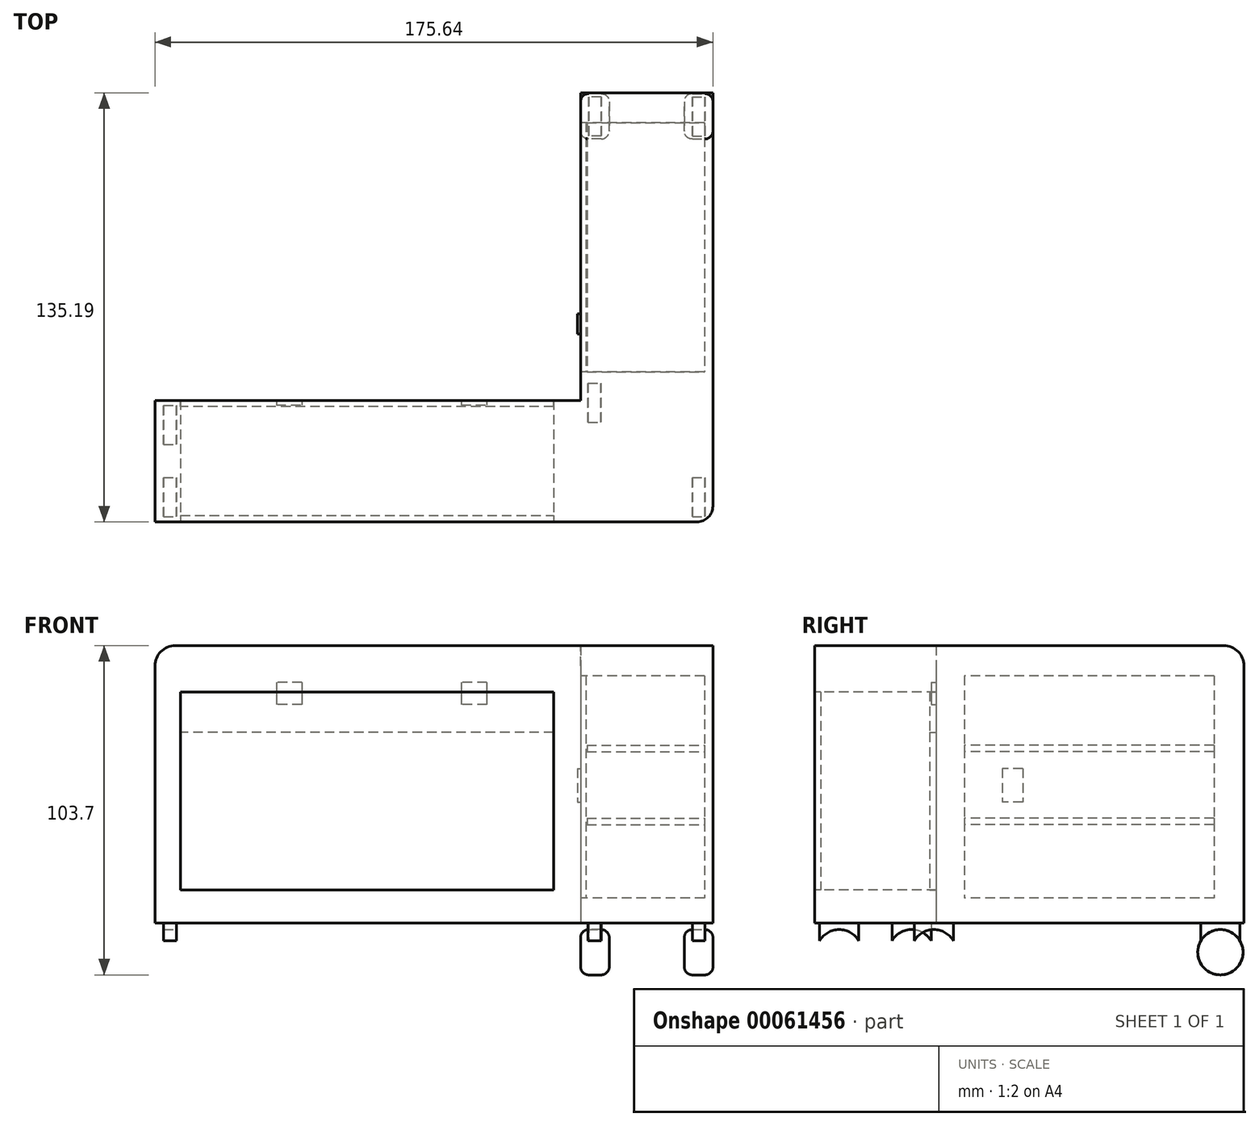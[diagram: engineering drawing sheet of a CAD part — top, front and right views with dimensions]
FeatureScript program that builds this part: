
annotation { "Feature Type Name" : "Feature", "Feature Type Description" : "" }
export const myFeature = defineFeature(function(context is Context, id is Id, definition is map)
    precondition{}
    {
        {
            var Q0;
            Q0=qCreatedBy(makeId("Front.planeOp"),FACE);
            var sketch = newSketch(context, id + "F0", { "sketchPlane" : qUnion([Q0])});
            skLineSegment(sketch, "E0.rect.bottom", {"start": v(-60.65, 49.22) * mm, "end": v(67, 49.22) * mm});
            skLineSegment(sketch, "E0.rect.left", {"start": v(-67, 42.87) * mm, "end": v(-67, -38.15) * mm});
            skLineSegment(sketch, "E0.rect.right", {"start": v(67, 49.22) * mm, "end": v(67, -38.15) * mm});
            skPoint(sketch, "E0.rect.middle", {"position": v(0, 0) * mm});
            skPoint(sketch, "E1.visualSharp", {"position": v(-67, 49.22) * mm});
            skArc(sketch, "E1.filletArc", {"start": v(-60.65, 49.22) * mm, "mid": v(-65.14, 47.36) * mm, "end": v(-67, 42.87) * mm});
            skLineSegment(sketch, "E2", {"start": v(-67, -38.15) * mm, "end": v(67, -38.15) * mm});
            skPoint(sketch, "E0.rect.top.start.orphan", {"position": v(-67, -49.22) * mm});
            skPoint(sketch, "E3.orphan", {"position": v(67, -49.22) * mm});
            skSolve(sketch);
        }
        {
            var Q0;
            Q0=makeQuery(id+"F0.imprint","IMPRINT",FACE,{"disambiguationData":[TD([[makeQuery(id+"F0.imprint","IMPRINT",EDGE,{"derivedFrom":sQuery(id+"F0.wireOp",EDGE,"E0.rect.bottom")}),-1.0]])]});
            extrude(context, id + "F1", {"entities" : qUnion([Q0]), "depth" : 38.28 * mm});
        }
        {
            var Q0;
            Q0=makeQuery(id+"F1.opExtrude","CAP_FACE",FACE,{"disambiguationData":[OSD([sQuery(id+"F0.wireOp",EDGE,"E0.rect.bottom"),sQuery(id+"F0.wireOp",EDGE,"E0.rect.left"),sQuery(id+"F0.wireOp",EDGE,"E0.rect.right"),sQuery(id+"F0.wireOp",EDGE,"E1.filletArc"),sQuery(id+"F0.wireOp",EDGE,"E2")])],"isStart":false});
            var sketch = newSketch(context, id + "F2", { "sketchPlane" : qUnion([Q0])});
            skLineSegment(sketch, "E4.bottom", {"start": v(-58.97, 34.69) * mm, "end": v(58.47, 34.69) * mm});
            skLineSegment(sketch, "E4.top", {"start": v(-58.97, -27.7) * mm, "end": v(58.47, -27.7) * mm});
            skLineSegment(sketch, "E4.left", {"start": v(-58.97, 34.69) * mm, "end": v(-58.97, -27.7) * mm});
            skLineSegment(sketch, "E4.right", {"start": v(58.47, 34.69) * mm, "end": v(58.47, -27.7) * mm});
            skSolve(sketch);
        }
        {
            var Q0;
            Q0 = qSketchRegion(id + "F2", true);
            extrude(context, id + "F3", {"entities" : qUnion([Q0]), "operationType" : NewBodyOperationType.REMOVE, "endBound" : BoundingType.THROUGH_ALL, "oppositeDirection" : true, "depth" : 25 * mm});
        }
        {
            var Q0;
            Q0=makeQuery(id+"F1.opExtrude","CAP_FACE",FACE,{"disambiguationData":[OSD([sQuery(id+"F0.wireOp",EDGE,"E0.rect.bottom"),sQuery(id+"F0.wireOp",EDGE,"E0.rect.left"),sQuery(id+"F0.wireOp",EDGE,"E0.rect.right"),sQuery(id+"F0.wireOp",EDGE,"E1.filletArc"),sQuery(id+"F0.wireOp",EDGE,"E2")])],"isStart":false});
            var sketch = newSketch(context, id + "F4", { "sketchPlane" : qUnion([Q0])});
            skLineSegment(sketch, "E5.0", {"start": v(-58.97, 34.69) * mm, "end": v(58.47, 34.69) * mm});
            skLineSegment(sketch, "E6.0", {"start": v(-58.97, 34.69) * mm, "end": v(-58.97, -27.7) * mm});
            skLineSegment(sketch, "E7.0", {"start": v(-58.97, -27.7) * mm, "end": v(58.47, -27.7) * mm});
            skLineSegment(sketch, "E8.0", {"start": v(58.47, 34.69) * mm, "end": v(58.47, -27.7) * mm});
            skSolve(sketch);
        }
        {
            var Q0;
            Q0=makeQuery(id+"F4.imprint","IMPRINT",FACE,{"disambiguationData":[TD([[makeQuery(id+"F4.imprint","IMPRINT",EDGE,{"derivedFrom":sQuery(id+"F4.wireOp",EDGE,"E5.0")}),-1.0]])]});
            extrude(context, id + "F5", {"entities" : qUnion([Q0]), "oppositeDirection" : true, "depth" : 2 * mm});
        }
        {
            var Q0;
            Q0=makeQuery(id+"F1.opExtrude","CAP_FACE",FACE,{"disambiguationData":[OSD([sQuery(id+"F0.wireOp",EDGE,"E0.rect.bottom"),sQuery(id+"F0.wireOp",EDGE,"E0.rect.left"),sQuery(id+"F0.wireOp",EDGE,"E0.rect.right"),sQuery(id+"F0.wireOp",EDGE,"E1.filletArc"),sQuery(id+"F0.wireOp",EDGE,"E2")])],"isStart":true});
            var sketch = newSketch(context, id + "F6", { "sketchPlane" : qUnion([Q0])});
            skLineSegment(sketch, "E9.0", {"start": v(-58.47, 21.87) * mm, "end": v(-58.47, -27.7) * mm});
            skLineSegment(sketch, "E10.0", {"start": v(58.97, -27.7) * mm, "end": v(-58.47, -27.7) * mm});
            skLineSegment(sketch, "E11.0", {"start": v(58.97, 21.87) * mm, "end": v(58.97, -27.7) * mm});
            skLineSegment(sketch, "E12", {"start": v(-58.47, 21.87) * mm, "end": v(58.97, 21.87) * mm});
            skPoint(sketch, "E13.0.end.orphan", {"position": v(-58.47, 34.69) * mm});
            skPoint(sketch, "E14.orphan", {"position": v(58.97, 34.69) * mm});
            skSolve(sketch);
        }
        {
            var Q0;
            Q0=makeQuery(id+"F6.imprint","IMPRINT",FACE,{"disambiguationData":[TD([[makeQuery(id+"F6.imprint","IMPRINT",EDGE,{"derivedFrom":sQuery(id+"F6.wireOp",EDGE,"E9.0")}),1.0]])]});
            extrude(context, id + "F7", {"entities" : qUnion([Q0]), "oppositeDirection" : true, "depth" : 2 * mm});
        }
        {
            var Q0;
            Q0=makeQuery(id+"F1.opExtrude","CAP_FACE",FACE,{"disambiguationData":[OSD([sQuery(id+"F0.wireOp",EDGE,"E0.rect.bottom"),sQuery(id+"F0.wireOp",EDGE,"E0.rect.left"),sQuery(id+"F0.wireOp",EDGE,"E0.rect.right"),sQuery(id+"F0.wireOp",EDGE,"E1.filletArc"),sQuery(id+"F0.wireOp",EDGE,"E2")])],"isStart":true});
            var sketch = newSketch(context, id + "F8", { "sketchPlane" : qUnion([Q0])});
            skLineSegment(sketch, "E15.0", {"start": v(58.97, 34.69) * mm, "end": v(-58.47, 34.69) * mm});
            skLineSegment(sketch, "E16.0", {"start": v(-58.47, 34.69) * mm, "end": v(-58.47, 21.87) * mm});
            skLineSegment(sketch, "E17.0", {"start": v(-58.47, 21.87) * mm, "end": v(58.97, 21.87) * mm});
            skLineSegment(sketch, "E18.0", {"start": v(58.97, 34.69) * mm, "end": v(58.97, 21.87) * mm});
            skPoint(sketch, "E19.orphan", {"position": v(-58.47, -27.7) * mm});
            skPoint(sketch, "E20.orphan", {"position": v(58.97, -27.7) * mm});
            skSolve(sketch);
        }
        {
            var Q0;
            Q0=makeQuery(id+"F8.imprint","IMPRINT",FACE,{"disambiguationData":[TD([[makeQuery(id+"F8.imprint","IMPRINT",EDGE,{"derivedFrom":sQuery(id+"F8.wireOp",EDGE,"E15.0")}),1.0]])]});
            extrude(context, id + "F9", {"entities" : qUnion([Q0]), "oppositeDirection" : true, "depth" : 2 * mm});
        }
        {
            var Q0;
            Q0=makeQuery(id+"F1.opExtrude","CAP_FACE",FACE,{"disambiguationData":[OSD([sQuery(id+"F0.wireOp",EDGE,"E0.rect.bottom"),sQuery(id+"F0.wireOp",EDGE,"E0.rect.left"),sQuery(id+"F0.wireOp",EDGE,"E0.rect.right"),sQuery(id+"F0.wireOp",EDGE,"E1.filletArc"),sQuery(id+"F0.wireOp",EDGE,"E2")])],"isStart":true});
            cPlane(context, id + "F10", {"entities" : qUnion([Q0]), "cplaneType" : CPlaneType.OFFSET, "offset" : 0 * mm, "width" : 150 * mm, "height" : 150 * mm});
        }
        {
            var Q0;
            Q0=qCreatedBy(id+"F10.planeOp",FACE);
            var sketch = newSketch(context, id + "F11", { "sketchPlane" : qUnion([Q0])});
            skLineSegment(sketch, "E21.bottom", {"start": v(-37.46, 37.7) * mm, "end": v(-29.46, 37.7) * mm});
            skLineSegment(sketch, "E21.top", {"start": v(-37.46, 30.7) * mm, "end": v(-29.46, 30.7) * mm});
            skLineSegment(sketch, "E21.left", {"start": v(-37.46, 37.7) * mm, "end": v(-37.46, 30.7) * mm});
            skLineSegment(sketch, "E21.right", {"start": v(-29.46, 37.7) * mm, "end": v(-29.46, 30.7) * mm});
            skPoint(sketch, "E22.firstSnap0", {"position": v(-33.46, 37.7) * mm});
            skLineSegment(sketch, "E22.bottom", {"start": v(20.75, 37.7) * mm, "end": v(28.75, 37.7) * mm});
            skLineSegment(sketch, "E22.top", {"start": v(20.75, 30.7) * mm, "end": v(28.75, 30.7) * mm});
            skLineSegment(sketch, "E22.left", {"start": v(20.75, 37.7) * mm, "end": v(20.75, 30.7) * mm});
            skLineSegment(sketch, "E22.right", {"start": v(28.75, 37.7) * mm, "end": v(28.75, 30.7) * mm});
            skSolve(sketch);
        }
        {
            var Q0;
            Q0=makeQuery(id+"F11.imprint","IMPRINT",FACE,{"disambiguationData":[TD([[makeQuery(id+"F11.imprint","IMPRINT",EDGE,{"derivedFrom":sQuery(id+"F11.wireOp",EDGE,"E21.bottom")}),-1.0]])]});
            var Q1;
            Q1=makeQuery(id+"F11.imprint","IMPRINT",FACE,{"disambiguationData":[TD([[makeQuery(id+"F11.imprint","IMPRINT",EDGE,{"derivedFrom":sQuery(id+"F11.wireOp",EDGE,"E22.bottom")}),-1.0]])]});
            extrude(context, id + "F12", {"entities" : qUnion([Q0, Q1]), "operationType" : NewBodyOperationType.REMOVE, "oppositeDirection" : true, "depth" : 1.5 * mm});
        }
        {
            var Q0;
            Q0=qCreatedBy(id+"F10.planeOp",FACE);
            var sketch = newSketch(context, id + "F13", { "sketchPlane" : qUnion([Q0])});
            skLineSegment(sketch, "E23.0", {"start": v(-37.46, 37.7) * mm, "end": v(-29.46, 37.7) * mm});
            skLineSegment(sketch, "E24.0", {"start": v(-37.46, 37.7) * mm, "end": v(-37.46, 34.69) * mm});
            skLineSegment(sketch, "E25.0", {"start": v(-37.46, 34.69) * mm, "end": v(-37.46, 30.7) * mm});
            skLineSegment(sketch, "E26.0", {"start": v(-37.46, 30.7) * mm, "end": v(-29.46, 30.7) * mm});
            skLineSegment(sketch, "E27.0", {"start": v(-29.46, 34.69) * mm, "end": v(-29.46, 30.7) * mm});
            skLineSegment(sketch, "E28.0", {"start": v(-29.46, 37.7) * mm, "end": v(-29.46, 34.69) * mm});
            skLineSegment(sketch, "E29.0", {"start": v(20.75, 37.7) * mm, "end": v(20.75, 34.69) * mm});
            skLineSegment(sketch, "E30.0", {"start": v(20.75, 37.7) * mm, "end": v(28.75, 37.7) * mm});
            skLineSegment(sketch, "E31.0", {"start": v(28.75, 37.7) * mm, "end": v(28.75, 34.69) * mm});
            skLineSegment(sketch, "E32.0", {"start": v(28.75, 34.69) * mm, "end": v(28.75, 30.7) * mm});
            skLineSegment(sketch, "E33.0", {"start": v(20.75, 30.7) * mm, "end": v(28.75, 30.7) * mm});
            skLineSegment(sketch, "E34.0.0", {"start": v(20.75, 34.69) * mm, "end": v(20.75, 30.7) * mm});
            skLineSegment(sketch, "E34.0.2", {"start": v(28.75, 30.7) * mm, "end": v(28.75, 34.69) * mm});
            skSolve(sketch);
        }
        {
            var Q0;
            Q0=makeQuery(id+"F13.imprint","IMPRINT",FACE,{"disambiguationData":[TD([[makeQuery(id+"F13.imprint","IMPRINT",EDGE,{"derivedFrom":sQuery(id+"F13.wireOp",EDGE,"E23.0")}),-1.0]])]});
            var Q1;
            Q1=makeQuery(id+"F13.imprint","IMPRINT",FACE,{"disambiguationData":[TD([[makeQuery(id+"F13.imprint","IMPRINT",EDGE,{"derivedFrom":sQuery(id+"F13.wireOp",EDGE,"E29.0")}),1.0]])]});
            extrude(context, id + "F14", {"entities" : qUnion([Q0, Q1]), "oppositeDirection" : true, "depth" : 1.5 * mm});
        }
        {
            var Q0;
            Q0=makeQuery(id+"F1.opExtrude","SWEPT_FACE",FACE,{"disambiguationData":[OSD([sQuery(id+"F0.wireOp",EDGE,"E0.rect.right")])]});
            cPlane(context, id + "F15", {"entities" : qUnion([Q0]), "cplaneType" : CPlaneType.OFFSET, "offset" : 0 * mm, "width" : 150 * mm, "height" : 150 * mm});
        }
        {
            var Q0;
            Q0=qCreatedBy(id+"F15.planeOp",FACE);
            var sketch = newSketch(context, id + "F16", { "sketchPlane" : qUnion([Q0])});
            skLineSegment(sketch, "E35.0", {"start": v(-38.28, 49.22) * mm, "end": v(0, 49.22) * mm});
            skLineSegment(sketch, "E36.0", {"start": v(-38.28, 49.22) * mm, "end": v(-38.28, -38.15) * mm});
            skLineSegment(sketch, "E37.0", {"start": v(-38.28, -38.15) * mm, "end": v(0, -38.15) * mm});
            skLineSegment(sketch, "E38", {"start": v(0, 49.22) * mm, "end": v(90.56, 49.22) * mm});
            skLineSegment(sketch, "E39", {"start": v(96.9, -38.15) * mm, "end": v(0, -38.15) * mm});
            skLineSegment(sketch, "E40", {"start": v(96.9, 42.87) * mm, "end": v(96.9, -38.15) * mm});
            skPoint(sketch, "E41.visualSharp", {"position": v(96.9, 49.22) * mm});
            skArc(sketch, "E41.filletArc", {"start": v(96.9, 42.87) * mm, "mid": v(95.05, 47.36) * mm, "end": v(90.56, 49.22) * mm});
            skSolve(sketch);
        }
        {
            var Q0;
            Q0=makeQuery(id+"F16.imprint","IMPRINT",FACE,{"disambiguationData":[TD([[makeQuery(id+"F16.imprint","IMPRINT",EDGE,{"derivedFrom":sQuery(id+"F16.wireOp",EDGE,"E35.0")}),-1.0]])]});
            extrude(context, id + "F17", {"entities" : qUnion([Q0]), "operationType" : NewBodyOperationType.ADD, "depth" : 41.64 * mm});
        }
        {
            var Q0;
            Q0=makeQuery(id+"F17.opExtrude","CAP_EDGE",EDGE,{"disambiguationData":[OSD([sQuery(id+"F16.wireOp",EDGE,"E36.0")])],"isStart":false});
            fillet(context, id + "F18", {"entities" : qUnion([Q0]), "radius" : 5 * mm, "tangentPropagation" : true, "allowEdgeOverflow" : false});
        }
        {
            var Q0;
            Q0=makeQuery(id+"F17.opExtrude","CAP_FACE",FACE,{"disambiguationData":[OSD([sQuery(id+"F16.wireOp",EDGE,"E35.0"),sQuery(id+"F16.wireOp",EDGE,"E36.0"),sQuery(id+"F16.wireOp",EDGE,"E37.0"),sQuery(id+"F16.wireOp",EDGE,"E38"),sQuery(id+"F16.wireOp",EDGE,"E39"),sQuery(id+"F16.wireOp",EDGE,"E40"),sQuery(id+"F16.wireOp",EDGE,"E41.filletArc")])],"isStart":true});
            var sketch = newSketch(context, id + "F19", { "sketchPlane" : qUnion([Q0])});
            skLineSegment(sketch, "E42.bottom", {"start": v(-87.48, 39.73) * mm, "end": v(-8.92, 39.73) * mm});
            skLineSegment(sketch, "E42.top", {"start": v(-87.48, -30.33) * mm, "end": v(-8.92, -30.33) * mm});
            skLineSegment(sketch, "E42.left", {"start": v(-87.48, 39.73) * mm, "end": v(-87.48, -30.33) * mm});
            skLineSegment(sketch, "E42.right", {"start": v(-8.92, 39.73) * mm, "end": v(-8.92, -30.33) * mm});
            skSolve(sketch);
        }
        {
            var Q0;
            Q0 = qSketchRegion(id + "F19", true);
            extrude(context, id + "F20", {"entities" : qUnion([Q0]), "operationType" : NewBodyOperationType.REMOVE, "oppositeDirection" : true, "depth" : 39 * mm});
        }
        {
            var Q0;
            Q0=makeQuery(id+"F20.boolean.opBoolean","COPY",FACE,{"derivedFrom":makeQuery(id+"F20.opExtrude","CAP_FACE",FACE,{"disambiguationData":[OSD([sQuery(id+"F19.wireOp",EDGE,"E42.bottom"),sQuery(id+"F19.wireOp",EDGE,"E42.top"),sQuery(id+"F19.wireOp",EDGE,"E42.left"),sQuery(id+"F19.wireOp",EDGE,"E42.right")])],"isStart":false})});
            var sketch = newSketch(context, id + "F21", { "sketchPlane" : qUnion([Q0])});
            skLineSegment(sketch, "E43.rect.left", {"start": v(-87.48, 15.81) * mm, "end": v(-87.48, 17.81) * mm});
            skLineSegment(sketch, "E43.rect.right", {"start": v(-8.92, 15.81) * mm, "end": v(-8.92, 17.81) * mm});
            skPoint(sketch, "E43.rect.middle", {"position": v(-48.2, 16.81) * mm});
            skLineSegment(sketch, "E44.rect.left", {"start": v(-87.48, -5.19) * mm, "end": v(-87.48, -7.19) * mm});
            skLineSegment(sketch, "E44.rect.right", {"start": v(-8.92, -5.19) * mm, "end": v(-8.92, -7.19) * mm});
            skPoint(sketch, "E44.rect.middle", {"position": v(-48.2, -6.19) * mm});
            skPoint(sketch, "E45.orphan", {"position": v(-87.48, -6.19) * mm});
            skPoint(sketch, "E46.end.orphan", {"position": v(-8.92, -6.19) * mm});
            skPoint(sketch, "E47.orphan", {"position": v(-87.48, 16.81) * mm});
            skPoint(sketch, "E48.end.orphan", {"position": v(-8.92, 16.81) * mm});
            skLineSegment(sketch, "E49", {"start": v(-8.92, 17.81) * mm, "end": v(-8.92, 15.81) * mm});
            skLineSegment(sketch, "E50", {"start": v(-87.48, 17.81) * mm, "end": v(-87.48, 15.81) * mm});
            skLineSegment(sketch, "E51.bottom", {"start": v(-87.48, 17.81) * mm, "end": v(-8.92, 17.81) * mm});
            skLineSegment(sketch, "E51.top", {"start": v(-87.48, 15.81) * mm, "end": v(-8.92, 15.81) * mm});
            skLineSegment(sketch, "E51.left", {"start": v(-87.48, 17.81) * mm, "end": v(-87.48, 16.81) * mm});
            skLineSegment(sketch, "E52.bottom", {"start": v(-87.48, -5.19) * mm, "end": v(-8.92, -5.19) * mm});
            skLineSegment(sketch, "E52.top", {"start": v(-87.48, -7.19) * mm, "end": v(-8.92, -7.19) * mm});
            skSolve(sketch);
        }
        {
            var Q0;
            {var subQ0=sQuery(id+"F21.wireOp",EDGE,"E51.bottom");Q0=makeQuery(id+"F21.imprint","IMPRINT",FACE,{"disambiguationData":[TD([[makeQuery(id+"F21.imprint","IMPRINT",EDGE,{"derivedFrom":subQ0}),-1.0]])]});}
            var Q1;
            Q1=makeQuery(id+"F21.imprint","IMPRINT",FACE,{"disambiguationData":[TD([[makeQuery(id+"F21.imprint","IMPRINT",EDGE,{"derivedFrom":sQuery(id+"F21.wireOp",EDGE,"E52.bottom")}),-1.0]])]});
            extrude(context, id + "F22", {"entities" : qUnion([Q0, Q1]), "depth" : 37 * mm});
        }
        {
            var Q0;
            Q0=makeQuery(id+"F17.opExtrude","CAP_FACE",FACE,{"disambiguationData":[OSD([sQuery(id+"F16.wireOp",EDGE,"E35.0"),sQuery(id+"F16.wireOp",EDGE,"E36.0"),sQuery(id+"F16.wireOp",EDGE,"E37.0"),sQuery(id+"F16.wireOp",EDGE,"E38"),sQuery(id+"F16.wireOp",EDGE,"E39"),sQuery(id+"F16.wireOp",EDGE,"E40"),sQuery(id+"F16.wireOp",EDGE,"E41.filletArc")])],"isStart":true});
            var sketch = newSketch(context, id + "F23", { "sketchPlane" : qUnion([Q0])});
            skLineSegment(sketch, "E53.0", {"start": v(-87.48, 39.73) * mm, "end": v(-8.92, 39.73) * mm});
            skLineSegment(sketch, "E54.0", {"start": v(-87.48, 39.73) * mm, "end": v(-87.48, -30.33) * mm});
            skLineSegment(sketch, "E55.0", {"start": v(-87.48, -30.33) * mm, "end": v(-8.92, -30.33) * mm});
            skLineSegment(sketch, "E56.0", {"start": v(-8.92, 39.73) * mm, "end": v(-8.92, -30.33) * mm});
            skSolve(sketch);
        }
        {
            var Q0;
            Q0 = qSketchRegion(id + "F23", true);
            extrude(context, id + "F24", {"entities" : qUnion([Q0]), "oppositeDirection" : true, "depth" : 1.72 * mm});
        }
        {
            var Q0;
            Q0=makeQuery(id+"F24.opExtrude","CAP_FACE",FACE,{"disambiguationData":[OSD([sQuery(id+"F23.wireOp",EDGE,"E53.0"),sQuery(id+"F23.wireOp",EDGE,"E54.0"),sQuery(id+"F23.wireOp",EDGE,"E55.0"),sQuery(id+"F23.wireOp",EDGE,"E56.0")])],"isStart":true});
            var sketch = newSketch(context, id + "F25", { "sketchPlane" : qUnion([Q0])});
            skLineSegment(sketch, "E57.bottom", {"start": v(-27.26, 10.52) * mm, "end": v(-20.85, 10.52) * mm});
            skLineSegment(sketch, "E57.top", {"start": v(-27.26, 0) * mm, "end": v(-20.85, 0) * mm});
            skLineSegment(sketch, "E57.left", {"start": v(-27.26, 10.52) * mm, "end": v(-27.26, 0) * mm});
            skLineSegment(sketch, "E57.right", {"start": v(-20.85, 10.52) * mm, "end": v(-20.85, 0) * mm});
            skSolve(sketch);
        }
        {
            var Q0;
            Q0 = qSketchRegion(id + "F25", true);
            extrude(context, id + "F26", {"entities" : qUnion([Q0]), "operationType" : NewBodyOperationType.ADD, "depth" : 1 * mm});
        }
        {
            var Q0;
            Q0=makeQuery(id+"F17.opExtrude","CAP_FACE",FACE,{"disambiguationData":[OSD([sQuery(id+"F16.wireOp",EDGE,"E35.0"),sQuery(id+"F16.wireOp",EDGE,"E36.0"),sQuery(id+"F16.wireOp",EDGE,"E37.0"),sQuery(id+"F16.wireOp",EDGE,"E38"),sQuery(id+"F16.wireOp",EDGE,"E39"),sQuery(id+"F16.wireOp",EDGE,"E40"),sQuery(id+"F16.wireOp",EDGE,"E41.filletArc")])],"isStart":false});
            var sketch = newSketch(context, id + "F27", { "sketchPlane" : qUnion([Q0])});
            skCircle(sketch, "E58", {"center": v(89.48, -47.35) * mm, "radius": 7.14 * mm});
            skSolve(sketch);
        }
        {
            var Q0;
            Q0=makeQuery(id+"F27.imprint","IMPRINT",FACE,{"disambiguationData":[TD([[makeQuery(id+"F27.imprint","IMPRINT",EDGE,{"derivedFrom":sQuery(id+"F27.wireOp",EDGE,"E58")}),1.0]])]});
            extrude(context, id + "F28", {"entities" : qUnion([Q0]), "oppositeDirection" : true, "depth" : 9 * mm});
        }
        {
            var Q0;
            Q0=makeQuery(id+"F28.opExtrude","CAP_EDGE",EDGE,{"disambiguationData":[OSD([sQuery(id+"F27.wireOp",EDGE,"E58")])],"isStart":true});
            var Q1;
            Q1=makeQuery(id+"F28.opExtrude","CAP_EDGE",EDGE,{"disambiguationData":[OSD([sQuery(id+"F27.wireOp",EDGE,"E58")])],"isStart":false});
            fillet(context, id + "F29", {"entities" : qUnion([Q0, Q1]), "radius" : 2.5 * mm, "tangentPropagation" : true, "allowEdgeOverflow" : false});
        }
        {
            var Q0;
            Q0=makeQuery(id+"F28.opExtrude","CAP_FACE",FACE,{"disambiguationData":[OSD([sQuery(id+"F27.wireOp",EDGE,"E58")])],"isStart":true});
            cPlane(context, id + "F30", {"entities" : qUnion([Q0]), "cplaneType" : CPlaneType.OFFSET, "offset" : 2.5 * mm, "oppositeDirection" : true, "width" : 150 * mm, "height" : 150 * mm});
        }
        {
            var Q0;
            Q0=qCreatedBy(id+"F30.planeOp",FACE);
            var sketch = newSketch(context, id + "F31", { "sketchPlane" : qUnion([Q0])});
            skArc(sketch, "E59.0", {"start": v(95.63, -43.73) * mm, "mid": v(89.48, -40.2) * mm, "end": v(83.32, -43.73) * mm});
            skLineSegment(sketch, "E60.0", {"start": v(83.32, -38.15) * mm, "end": v(95.63, -38.15) * mm});
            skLineSegment(sketch, "E61", {"start": v(83.32, -38.15) * mm, "end": v(83.32, -43.73) * mm});
            skLineSegment(sketch, "E62", {"start": v(95.63, -43.73) * mm, "end": v(95.63, -38.15) * mm});
            skPoint(sketch, "E63.orphan", {"position": v(-33.28, -38.15) * mm});
            skPoint(sketch, "E64.orphan", {"position": v(96.9, -38.15) * mm});
            skSolve(sketch);
        }
        {
            var Q0;
            Q0=makeQuery(id+"F31.imprint","IMPRINT",FACE,{"disambiguationData":[TD([[makeQuery(id+"F31.imprint","IMPRINT",EDGE,{"derivedFrom":sQuery(id+"F31.wireOp",EDGE,"E59.0")}),-1.0]])]});
            extrude(context, id + "F32", {"entities" : qUnion([Q0]), "oppositeDirection" : true, "depth" : 4 * mm});
        }
        {
            var Q0;
            Q0=makeQuery(id+"F17.opExtrude","SWEPT_FACE",FACE,{"disambiguationData":[OSD([sQuery(id+"F16.wireOp",EDGE,"E40")])]});
            var sketch = newSketch(context, id + "F33", { "sketchPlane" : qUnion([Q0])});
            skLineSegment(sketch, "E65.0", {"start": v(-108.64, -38.15) * mm, "end": v(-67, -38.15) * mm, "construction": true});
            skLineSegment(sketch, "E66", {"start": v(-87.82, -38.15) * mm, "end": v(-87.82, 27.49) * mm, "construction": true});
            skSolve(sketch);
        }
        {
            var Q0;
            Q0=sQuery(id+"F33.wireOp",EDGE,"E66");
            cPlane(context, id + "F34", {"entities" : qUnion([Q0]), "cplaneType" : CPlaneType.LINE_ANGLE, "offset" : 150 * mm, "angle" : 0 * degree, "width" : 150 * mm, "height" : 150 * mm});
        }
        {
            var Q0;
            Q0=makeQuery(id+"F28.opExtrude","SWEPT_BODY",BODY,{"disambiguationData":[OSD([sQuery(id+"F27.wireOp",EDGE,"E58")])]});
            var Q1;
            Q1=makeQuery(id+"F32.opExtrude","SWEPT_BODY",BODY,{"disambiguationData":[OSD([sQuery(id+"F31.wireOp",EDGE,"E59.0"),sQuery(id+"F31.wireOp",EDGE,"E60.0"),sQuery(id+"F31.wireOp",EDGE,"E61"),sQuery(id+"F31.wireOp",EDGE,"E62")])]});
            var Q2;
            Q2=qCreatedBy(id+"F34.planeOp",FACE);
            mirror(context, id + "F35", {"entities" : qUnion([Q0, Q1]), "mirrorPlane" : qUnion([Q2])});
        }
        {
            var Q0;
            Q0=makeQuery(id+"F32.opExtrude","SWEPT_BODY",BODY,{"disambiguationData":[OSD([sQuery(id+"F31.wireOp",EDGE,"E59.0"),sQuery(id+"F31.wireOp",EDGE,"E60.0"),sQuery(id+"F31.wireOp",EDGE,"E61"),sQuery(id+"F31.wireOp",EDGE,"E62")])]});
            transform(context, id + "F36", {"entities" : qUnion([Q0]), "transformType" : TransformType.TRANSLATION_3D, "dx" : 0 * mm, "dy" : -120 * mm, "dz" : 0 * mm, "makeCopy" : true});
        }
        {
            var Q0;
            Q0=makeQuery(id+"F36.opPattern","COPY",BODY,{"derivedFrom":makeQuery(id+"F32.opExtrude","SWEPT_BODY",BODY,{"disambiguationData":[OSD([sQuery(id+"F31.wireOp",EDGE,"E59.0"),sQuery(id+"F31.wireOp",EDGE,"E60.0"),sQuery(id+"F31.wireOp",EDGE,"E61"),sQuery(id+"F31.wireOp",EDGE,"E62")])]}),"instanceName":"1"});
            transform(context, id + "F37", {"entities" : qUnion([Q0]), "transformType" : TransformType.TRANSLATION_3D, "dx" : -166.4 * mm, "dy" : 0 * mm, "dz" : 0 * mm, "makeCopy" : true});
        }
        {
            var Q0;
            Q0=makeQuery(id+"F1.opExtrude","SWEPT_FACE",FACE,{"disambiguationData":[OSD([sQuery(id+"F0.wireOp",EDGE,"E0.rect.left")])]});
            var sketch = newSketch(context, id + "F38", { "sketchPlane" : qUnion([Q0])});
            skLineSegment(sketch, "E67.0", {"start": v(38.28, -38.15) * mm, "end": v(0, -38.15) * mm, "construction": true});
            skLineSegment(sketch, "E68", {"start": v(19.14, -38.15) * mm, "end": v(19.14, 29.3) * mm, "construction": true});
            skSolve(sketch);
        }
        {
            var Q0;
            Q0=sQuery(id+"F38.wireOp",EDGE,"E68");
            cPlane(context, id + "F39", {"entities" : qUnion([Q0]), "cplaneType" : CPlaneType.LINE_ANGLE, "offset" : 150 * mm, "angle" : 90 * degree, "width" : 150 * mm, "height" : 150 * mm});
        }
        {
            var Q0;
            Q0=makeQuery(id+"F37.opPattern","COPY",BODY,{"derivedFrom":makeQuery(id+"F36.opPattern","COPY",BODY,{"derivedFrom":makeQuery(id+"F32.opExtrude","SWEPT_BODY",BODY,{"disambiguationData":[OSD([sQuery(id+"F31.wireOp",EDGE,"E59.0"),sQuery(id+"F31.wireOp",EDGE,"E60.0"),sQuery(id+"F31.wireOp",EDGE,"E61"),sQuery(id+"F31.wireOp",EDGE,"E62")])]}),"instanceName":"1"}),"instanceName":"1"});
            var Q1;
            Q1=qCreatedBy(id+"F39.planeOp",FACE);
            mirror(context, id + "F40", {"entities" : qUnion([Q0]), "mirrorPlane" : qUnion([Q1])});
        }
        {
            var Q0;
            Q0=makeQuery(id+"F40.opPattern","COPY",BODY,{"derivedFrom":makeQuery(id+"F37.opPattern","COPY",BODY,{"derivedFrom":makeQuery(id+"F36.opPattern","COPY",BODY,{"derivedFrom":makeQuery(id+"F32.opExtrude","SWEPT_BODY",BODY,{"disambiguationData":[OSD([sQuery(id+"F31.wireOp",EDGE,"E59.0"),sQuery(id+"F31.wireOp",EDGE,"E60.0"),sQuery(id+"F31.wireOp",EDGE,"E61"),sQuery(id+"F31.wireOp",EDGE,"E62")])]}),"instanceName":"1"}),"instanceName":"1"}),"instanceName":"1"});
            transform(context, id + "F41", {"entities" : qUnion([Q0]), "transformType" : TransformType.TRANSLATION_3D, "dx" : 133.58 * mm, "dy" : 7.02 * mm, "dz" : 0 * mm, "makeCopy" : true});
        }
    });
